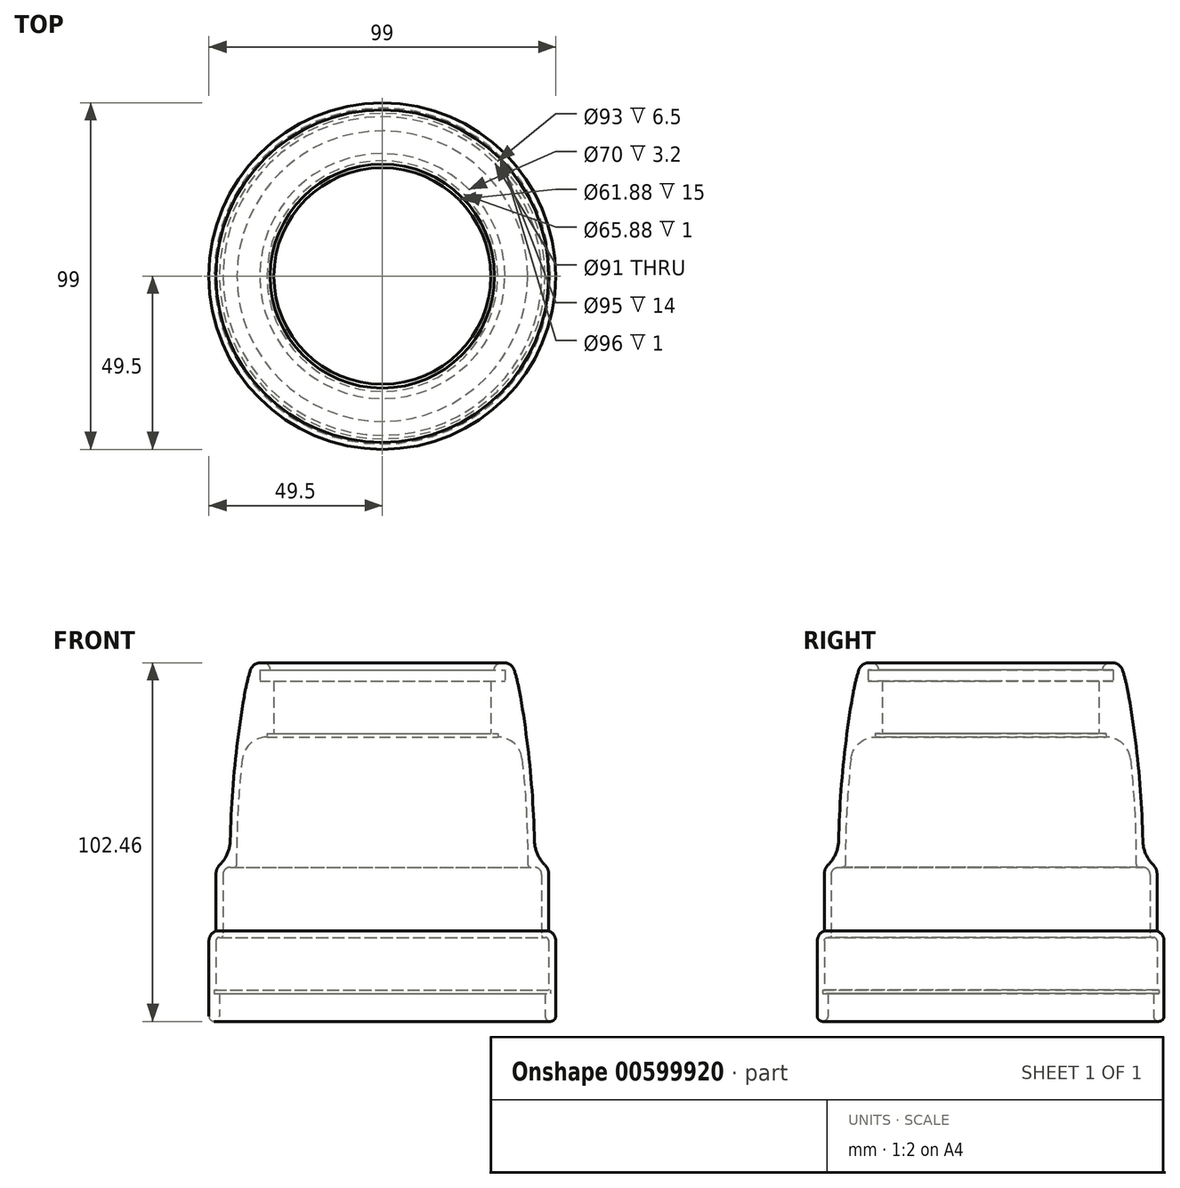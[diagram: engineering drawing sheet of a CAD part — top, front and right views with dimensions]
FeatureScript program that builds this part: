
annotation { "Feature Type Name" : "Feature", "Feature Type Description" : "" }
export const myFeature = defineFeature(function(context is Context, id is Id, definition is map)
    precondition{}
    {
        {
            var Q0;
            Q0=qCreatedBy(makeId("Front.planeOp"),FACE);
            var sketch = newSketch(context, id + "F0", { "sketchPlane" : qUnion([Q0])});
            skLineSegment(sketch, "E0.2", {"start": v(47.5, -21.89) * mm, "end": v(47.5, -7.89) * mm});
            skLineSegment(sketch, "E0.3", {"start": v(46.5, -6.89) * mm, "end": v(46, -6.89) * mm});
            skLineSegment(sketch, "E0.4", {"start": v(45.5, -6.39) * mm, "end": v(45.5, 11.11) * mm});
            skLineSegment(sketch, "E0.5", {"start": v(43.5, 13.11) * mm, "end": v(42.5, 13.11) * mm});
            skArc(sketch, "E1.filletArc", {"start": v(45.5, -6.39) * mm, "mid": v(45.65, -6.74) * mm, "end": v(46, -6.89) * mm});
            skArc(sketch, "E2.filletArc", {"start": v(47.5, -7.89) * mm, "mid": v(47.2, -7.18) * mm, "end": v(46.5, -6.89) * mm});
            skArc(sketch, "E3.filletArc", {"start": v(45.5, 11.11) * mm, "mid": v(44.91, 12.53) * mm, "end": v(43.5, 13.11) * mm});
            skArc(sketch, "E4.filletArc", {"start": v(41.5, 14.11) * mm, "mid": v(41.8, 13.4) * mm, "end": v(42.5, 13.11) * mm});
            skLineSegment(sketch, "E5", {"start": v(46.5, -22.89) * mm, "end": v(48, -22.89) * mm});
            skLineSegment(sketch, "E6", {"start": v(48, -22.89) * mm, "end": v(48, -21.89) * mm});
            skLineSegment(sketch, "E7", {"start": v(48, -21.89) * mm, "end": v(47.5, -21.89) * mm});
            skArc(sketch, "E8", {"start": v(41.5, 14.11) * mm, "mid": v(41.1, 29.14) * mm, "end": v(39.9, 44.11) * mm});
            skPoint(sketch, "E9.visualSharp", {"position": v(40.23, 40.86) * mm});
            skArc(sketch, "E9.filletArc", {"start": v(39.9, 44.11) * mm, "mid": v(37.62, 48.58) * mm, "end": v(32.94, 50.37) * mm});
            skLineSegment(sketch, "E10", {"start": v(46.5, -22.89) * mm, "end": v(46.5, -30.89) * mm});
            skLineSegment(sketch, "E11", {"start": v(46.5, -30.89) * mm, "end": v(49.5, -30.89) * mm});
            skLineSegment(sketch, "E12", {"start": v(49.5, -30.89) * mm, "end": v(49.5, -7.89) * mm});
            skLineSegment(sketch, "E13.0", {"start": v(47.5, -5.06) * mm, "end": v(47.5, 11.11) * mm});
            skArc(sketch, "E13.1", {"start": v(49.5, -7.89) * mm, "mid": v(48.95, -6.15) * mm, "end": v(47.5, -5.06) * mm});
            skArc(sketch, "E14.0", {"start": v(43.42, 20.76) * mm, "mid": v(42.18, 41.43) * mm, "end": v(39.44, 61.95) * mm});
            skArc(sketch, "E14.1", {"start": v(47.5, 11.11) * mm, "mid": v(47.2, 12.64) * mm, "end": v(46.33, 13.94) * mm});
            skPoint(sketch, "E15.visualSharp", {"position": v(43.5, 15.11) * mm});
            skArc(sketch, "E15.filletArc", {"start": v(43.42, 20.76) * mm, "mid": v(44.22, 17.07) * mm, "end": v(46.33, 13.94) * mm});
            skLineSegment(sketch, "E16", {"start": v(32.94, 50.37) * mm, "end": v(32.94, 51.37) * mm});
            skLineSegment(sketch, "E17", {"start": v(32.94, 51.37) * mm, "end": v(30.94, 51.37) * mm});
            skLineSegment(sketch, "E18", {"start": v(30.94, 66.37) * mm, "end": v(35, 66.37) * mm});
            skLineSegment(sketch, "E19", {"start": v(35, 66.37) * mm, "end": v(35, 69.57) * mm});
            skLineSegment(sketch, "E20", {"start": v(35, 69.57) * mm, "end": v(32, 69.57) * mm});
            skLineSegment(sketch, "E21", {"start": v(32, 69.57) * mm, "end": v(32, 69.57) * mm});
            skLineSegment(sketch, "E22", {"start": v(34, 71.57) * mm, "end": v(34.81, 71.57) * mm});
            skArc(sketch, "E23", {"start": v(39.44, 61.95) * mm, "mid": v(38.68, 65.72) * mm, "end": v(37.68, 69.43) * mm});
            skPoint(sketch, "E24.visualSharp", {"position": v(37, 71.57) * mm});
            skArc(sketch, "E24.filletArc", {"start": v(37.68, 69.43) * mm, "mid": v(36.6, 70.98) * mm, "end": v(34.81, 71.57) * mm});
            skPoint(sketch, "E25.visualSharp", {"position": v(32, 71.57) * mm});
            skArc(sketch, "E25.filletArc", {"start": v(34, 71.57) * mm, "mid": v(32.59, 70.98) * mm, "end": v(32, 69.57) * mm});
            skLineSegment(sketch, "E26", {"start": v(30.94, 51.37) * mm, "end": v(30.94, 66.37) * mm});
            skLineSegment(sketch, "E27", {"start": v(0, 0) * mm, "end": v(0, 38.98) * mm, "construction": true});
            skSolve(sketch);
        }
        {
            var Q0;
            Q0 = qSketchRegion(id + "F0", true);
            var Q1;
            Q1=sQuery(id+"F0.wireOp",EDGE,"E27");
            revolve(context, id + "F1", {"entities" : qUnion([Q0]), "axis" : qUnion([Q1]), "revolveType" : RevolveType.FULL});
        }
        {
            var Q0;
            Q0=makeQuery(id+"F1.opRevolve","SWEPT_EDGE",EDGE,{"disambiguationData":[OSD([sQuery(id+"F0.wireOp",EDGE,"E11"),sQuery(id+"F0.wireOp",EDGE,"E12")])]});
            var Q1;
            Q1=makeQuery(id+"F1.opRevolve","SWEPT_EDGE",EDGE,{"disambiguationData":[OSD([sQuery(id+"F0.wireOp",EDGE,"E10"),sQuery(id+"F0.wireOp",EDGE,"E11")])]});
            fillet(context, id + "F2", {"entities" : qUnion([Q0, Q1]), "radius" : 1.5 * mm, "tangentPropagation" : true, "allowEdgeOverflow" : false});
        }
    });
